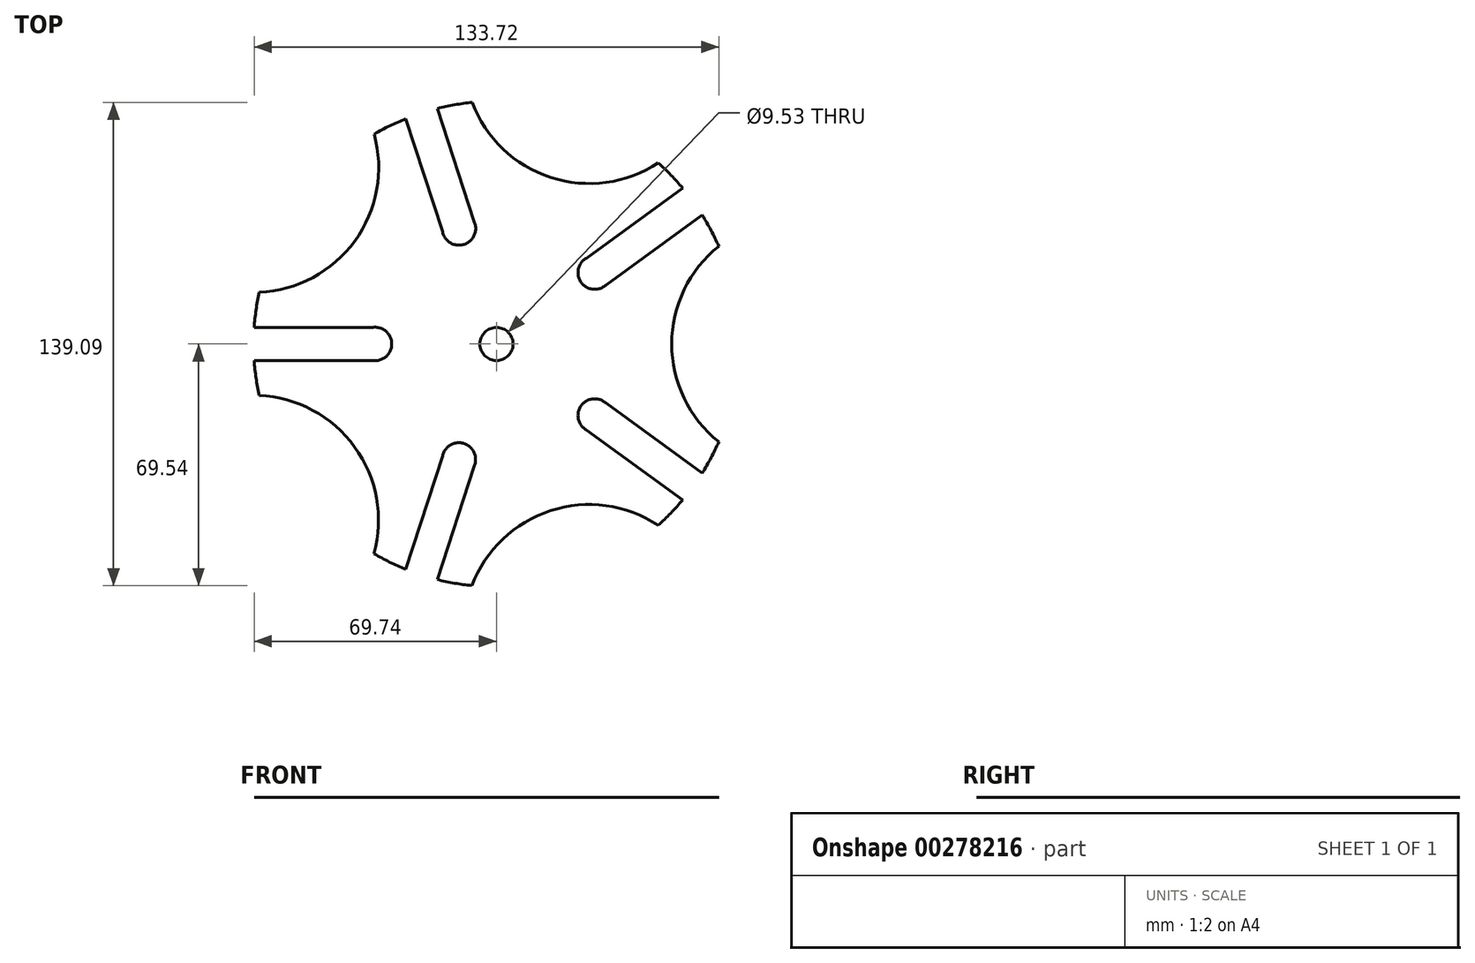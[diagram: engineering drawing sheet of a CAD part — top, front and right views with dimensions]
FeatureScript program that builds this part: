
annotation { "Feature Type Name" : "Feature", "Feature Type Description" : "" }
export const myFeature = defineFeature(function(context is Context, id is Id, definition is map)
    precondition{}
    {
        {
            var Q0;
            Q0=qCreatedBy(makeId("Top.planeOp"),FACE);
            var sketch = newSketch(context, id + "F0", { "sketchPlane" : qUnion([Q0])});
            skLineSegment(sketch, "E0", {"start": v(0, 0) * mm, "end": v(56.55, 41.08) * mm});
            skLineSegment(sketch, "E1", {"start": v(56.55, 41.08) * mm, "end": v(86.44, 0) * mm});
            skLineSegment(sketch, "E2", {"start": v(86.44, 0) * mm, "end": v(0, 0) * mm});
            skArc(sketch, "E3", {"start": v(63.98, 28.15) * mm, "mid": v(-69.9, 0) * mm, "end": v(63.98, -28.15) * mm});
            skArc(sketch, "E4", {"start": v(63.98, 28.15) * mm, "mid": v(50.43, 0) * mm, "end": v(63.98, -28.15) * mm});
            skLineSegment(sketch, "E5.0", {"start": v(25.9, 24.71) * mm, "end": v(53.62, 44.85) * mm});
            skLineSegment(sketch, "E6.MirrorCS", {"start": v(31.5, 16.98) * mm, "end": v(59.23, 37.12) * mm});
            skArc(sketch, "E7", {"start": v(25.9, 24.71) * mm, "mid": v(24.4, 17.72) * mm, "end": v(31.5, 16.98) * mm});
            skArc(sketch, "E8.MirrorCS", {"start": v(46.55, 52.15) * mm, "mid": v(15.6, 47.96) * mm, "end": v(-6.98, 69.55) * mm});
            skLineSegment(sketch, "E9.MirrorCS", {"start": v(56.55, 41.08) * mm, "end": v(26.72, 82.2) * mm});
            skLineSegment(sketch, "E10.MirrorCS", {"start": v(26.72, 82.2) * mm, "end": v(0, 0) * mm});
            skLineSegment(sketch, "E11.MirrorCS", {"start": v(-6.41, 35.21) * mm, "end": v(-17, 67.8) * mm});
            skLineSegment(sketch, "E12.MirrorCS", {"start": v(0, 0) * mm, "end": v(-21.58, 66.49) * mm});
            skLineSegment(sketch, "E13.MirrorCS", {"start": v(-15.5, 32.27) * mm, "end": v(-26.08, 64.86) * mm});
            skArc(sketch, "E14.MirrorCS", {"start": v(-6.41, 35.21) * mm, "mid": v(-9.3, 28.67) * mm, "end": v(-15.5, 32.27) * mm});
            skArc(sketch, "E15.MirrorCS", {"start": v(-68.3, 14.86) * mm, "mid": v(-40.8, 29.66) * mm, "end": v(-35.2, 60.4) * mm});
            skLineSegment(sketch, "E16.MirrorCS", {"start": v(-69.91, 50.83) * mm, "end": v(0, 0) * mm});
            skLineSegment(sketch, "E17.MirrorCS", {"start": v(-35.47, 4.8) * mm, "end": v(-69.74, 4.8) * mm});
            skLineSegment(sketch, "E18.MirrorCS", {"start": v(-35.47, -4.76) * mm, "end": v(-69.74, -4.75) * mm});
            skArc(sketch, "E19.MirrorCS", {"start": v(-35.47, -4.76) * mm, "mid": v(-30.15, 0.01) * mm, "end": v(-35.47, 4.8) * mm});
            skLineSegment(sketch, "E20.MirrorCS", {"start": v(0, 0) * mm, "end": v(-69.9, 0.03) * mm});
            skArc(sketch, "E21.MirrorCS", {"start": v(-68.32, -14.8) * mm, "mid": v(-40.82, -29.62) * mm, "end": v(-35.25, -60.36) * mm});
            skLineSegment(sketch, "E22.MirrorCS", {"start": v(-69.95, -50.77) * mm, "end": v(0, 0) * mm});
            skLineSegment(sketch, "E23.MirrorCS", {"start": v(-6.44, -35.2) * mm, "end": v(-17.05, -67.79) * mm});
            skLineSegment(sketch, "E24.MirrorCS", {"start": v(-15.52, -32.25) * mm, "end": v(-26.13, -64.83) * mm});
            skArc(sketch, "E25.MirrorCS", {"start": v(-15.52, -32.25) * mm, "mid": v(-9.33, -28.67) * mm, "end": v(-6.44, -35.2) * mm});
            skLineSegment(sketch, "E26.MirrorCS", {"start": v(0, 0) * mm, "end": v(-21.64, -66.47) * mm});
            skArc(sketch, "E27.MirrorCS", {"start": v(46.5, -52.19) * mm, "mid": v(15.55, -47.97) * mm, "end": v(-7.04, -69.54) * mm});
            skLineSegment(sketch, "E28.MirrorCS", {"start": v(26.65, -82.22) * mm, "end": v(0, 0) * mm});
            skLineSegment(sketch, "E29.MirrorCS", {"start": v(31.5, -17.01) * mm, "end": v(59.2, -37.17) * mm});
            skLineSegment(sketch, "E30.MirrorCS", {"start": v(25.87, -24.73) * mm, "end": v(53.58, -44.9) * mm});
            skArc(sketch, "E31.MirrorCS", {"start": v(31.5, -17.01) * mm, "mid": v(24.38, -17.74) * mm, "end": v(25.87, -24.73) * mm});
            skCircle(sketch, "E32", {"center": v(0, 0) * mm, "radius": 4.76 * mm});
            skSolve(sketch);
        }
        {
            var Q0;
            {var subQ0=sQuery(id+"F0.wireOp",EDGE,"E17.MirrorCS");Q0=makeQuery(id+"F0.imprint","IMPRINT",FACE,{"disambiguationData":[TD([[makeQuery(id+"F0.imprint","IMPRINT",EDGE,{"derivedFrom":subQ0}),-1.0]])]});}
            var Q1;
            {var subQ1=sQuery(id+"F0.wireOp",EDGE,"E13.MirrorCS");Q1=makeQuery(id+"F0.imprint","IMPRINT",FACE,{"disambiguationData":[TD([[makeQuery(id+"F0.imprint","IMPRINT",EDGE,{"derivedFrom":subQ1}),1.0]])]});}
            var Q2;
            {var subQ0=sQuery(id+"F0.wireOp",EDGE,"E11.MirrorCS");Q2=makeQuery(id+"F0.imprint","IMPRINT",FACE,{"disambiguationData":[TD([[makeQuery(id+"F0.imprint","IMPRINT",EDGE,{"derivedFrom":subQ0}),-1.0]])]});}
            var Q3;
            {var subQ1=sQuery(id+"F0.wireOp",EDGE,"E5.0");Q3=makeQuery(id+"F0.imprint","IMPRINT",FACE,{"disambiguationData":[TD([[makeQuery(id+"F0.imprint","IMPRINT",EDGE,{"derivedFrom":subQ1}),1.0]])]});}
            var Q4;
            {var subQ5=sQuery(id+"F0.wireOp",EDGE,"E6.MirrorCS");Q4=makeQuery(id+"F0.imprint","IMPRINT",FACE,{"disambiguationData":[TD([[makeQuery(id+"F0.imprint","IMPRINT",EDGE,{"derivedFrom":subQ5}),-1.0]])]});}
            var Q5;
            {var subQ8=sQuery(id+"F0.wireOp",EDGE,"E29.MirrorCS");Q5=makeQuery(id+"F0.imprint","IMPRINT",FACE,{"disambiguationData":[TD([[makeQuery(id+"F0.imprint","IMPRINT",EDGE,{"derivedFrom":subQ8}),1.0]])]});}
            var Q6;
            {var subQ5=sQuery(id+"F0.wireOp",EDGE,"E23.MirrorCS");Q6=makeQuery(id+"F0.imprint","IMPRINT",FACE,{"disambiguationData":[TD([[makeQuery(id+"F0.imprint","IMPRINT",EDGE,{"derivedFrom":subQ5}),1.0]])]});}
            var Q7;
            {var subQ9=sQuery(id+"F0.wireOp",EDGE,"E24.MirrorCS");Q7=makeQuery(id+"F0.imprint","IMPRINT",FACE,{"disambiguationData":[TD([[makeQuery(id+"F0.imprint","IMPRINT",EDGE,{"derivedFrom":subQ9}),-1.0]])]});}
            var Q8;
            {var subQ5=sQuery(id+"F0.wireOp",EDGE,"E18.MirrorCS");Q8=makeQuery(id+"F0.imprint","IMPRINT",FACE,{"disambiguationData":[TD([[makeQuery(id+"F0.imprint","IMPRINT",EDGE,{"derivedFrom":subQ5}),1.0]])]});}
            extrude(context, id + "F1", {"entities" : qUnion([Q0, Q1, Q2, Q3, Q4, Q5, Q6, Q7, Q8]), "depth" : 1 / 203.2 * mm});
        }
    });
